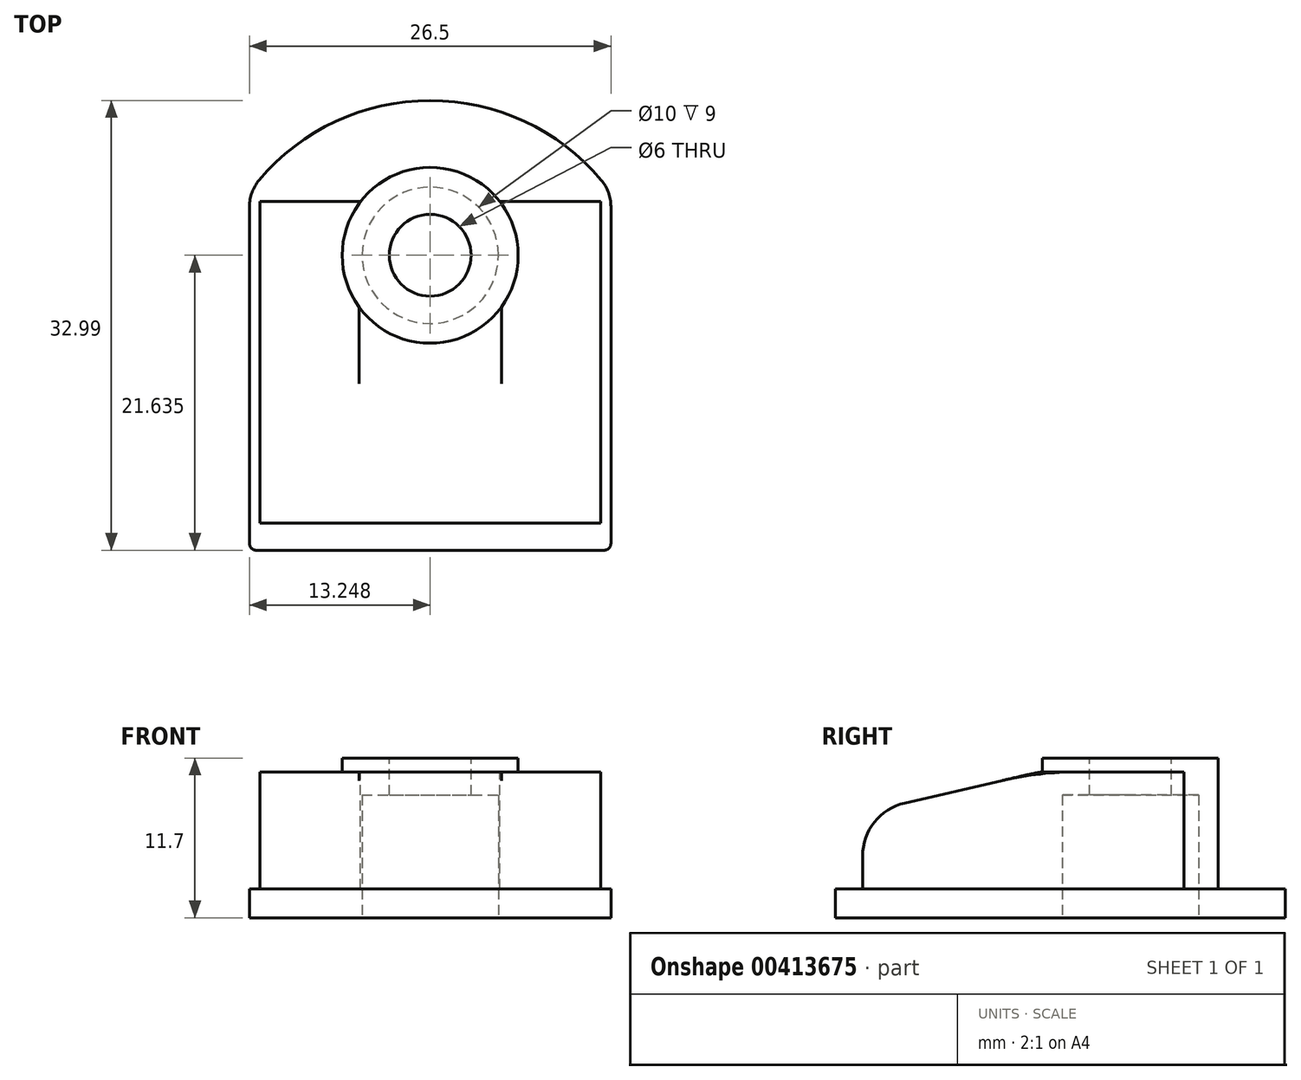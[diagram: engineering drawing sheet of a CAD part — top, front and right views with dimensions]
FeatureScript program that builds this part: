
annotation { "Feature Type Name" : "Feature", "Feature Type Description" : "" }
export const myFeature = defineFeature(function(context is Context, id is Id, definition is map)
    precondition{}
    {
        {
            var Q0;
            Q0=qCreatedBy(makeId("Top.planeOp"),FACE);
            var sketch = newSketch(context, id + "F0", { "sketchPlane" : qUnion([Q0])});
            skLineSegment(sketch, "E0", {"start": v(-15.11, -22.23) * mm, "end": v(11.39, -22.23) * mm});
            skLineSegment(sketch, "E1", {"start": v(11.39, -22.23) * mm, "end": v(11.39, 4.02) * mm});
            skLineSegment(sketch, "E2", {"start": v(-15.11, -22.23) * mm, "end": v(-15.11, 4.02) * mm});
            skArc(sketch, "E3", {"start": v(11.39, 4.02) * mm, "mid": v(-1.86, 10.76) * mm, "end": v(-15.11, 4.02) * mm});
            skSolve(sketch);
        }
        {
            var Q0;
            Q0 = qSketchRegion(id + "F0", true);
            extrude(context, id + "F1", {"entities" : qUnion([Q0]), "depth" : 2.1 * mm, "offsetDistance" : 25 * mm});
        }
        {
            var Q0;
            Q0=makeQuery(id+"F1.opExtrude","SWEPT_EDGE",EDGE,{"disambiguationData":[OSD([sQuery(id+"F0.wireOp",EDGE,"E0"),sQuery(id+"F0.wireOp",EDGE,"E2")])]});
            var Q1;
            Q1=makeQuery(id+"F1.opExtrude","SWEPT_EDGE",EDGE,{"disambiguationData":[OSD([sQuery(id+"F0.wireOp",EDGE,"E0"),sQuery(id+"F0.wireOp",EDGE,"E1")])]});
            fillet(context, id + "F2", {"entities" : qUnion([Q0, Q1]), "tangentPropagation" : true, "radius" : .5 * mm, "defaultsChanged" : true, "vertexSettings" : [], "allowEdgeOverflow" : false});
        }
        {
            var Q0;
            Q0=makeQuery(id+"F1.opExtrude","SWEPT_EDGE",EDGE,{"disambiguationData":[OSD([sQuery(id+"F0.wireOp",EDGE,"E1"),sQuery(id+"F0.wireOp",EDGE,"E3")])]});
            var Q1;
            Q1=makeQuery(id+"F1.opExtrude","SWEPT_EDGE",EDGE,{"disambiguationData":[OSD([sQuery(id+"F0.wireOp",EDGE,"E2"),sQuery(id+"F0.wireOp",EDGE,"E3")])]});
            fillet(context, id + "F3", {"entities" : qUnion([Q0, Q1]), "tangentPropagation" : true, "radius" : 3 * mm, "defaultsChanged" : true, "vertexSettings" : [], "allowEdgeOverflow" : false});
        }
        {
            var Q0;
            Q0=makeQuery(id+"F1.opExtrude","CAP_FACE",FACE,{"disambiguationData":[OSD([sQuery(id+"F0.wireOp",EDGE,"E0"),sQuery(id+"F0.wireOp",EDGE,"E1"),sQuery(id+"F0.wireOp",EDGE,"E2"),sQuery(id+"F0.wireOp",EDGE,"E3")])],"isStart":false});
            var sketch = newSketch(context, id + "F4", { "sketchPlane" : qUnion([Q0])});
            skLineSegment(sketch, "E4.0", {"start": v(10.64, -20.23) * mm, "end": v(10.64, 3.35) * mm});
            skLineSegment(sketch, "E4.2", {"start": v(-14.36, 3.35) * mm, "end": v(-14.36, -20.23) * mm});
            skLineSegment(sketch, "E5.0", {"start": v(-14.36, -20.23) * mm, "end": v(10.64, -20.23) * mm});
            skLineSegment(sketch, "E6", {"start": v(-14.36, 3.35) * mm, "end": v(10.64, 3.35) * mm});
            skSolve(sketch);
        }
        {
            var Q0;
            Q0 = qSketchRegion(id + "F4", true);
            extrude(context, id + "F5", {"entities" : qUnion([Q0]), "operationType" : NewBodyOperationType.ADD, "depth" : 8.6 * mm, "offsetDistance" : 25 * mm});
        }
        {
            var Q0;
            Q0=makeQuery(id+"F9.boolean.opBoolean","MERGE",FACE,{"derivedFrom":[makeQuery(id+"F5.opExtrude","CAP_FACE",FACE,{"disambiguationData":[OSD([sQuery(id+"F4.wireOp",EDGE,"E4.0"),sQuery(id+"F4.wireOp",EDGE,"E4.2"),sQuery(id+"F4.wireOp",EDGE,"E5.0"),sQuery(id+"F4.wireOp",EDGE,"E6")])],"isStart":false}),makeQuery(id+"F9.opExtrude","CAP_FACE",FACE,{"disambiguationData":[OSD([sQuery(id+"F8.wireOp",EDGE,"E8")])],"isStart":true})]});
            var sketch = newSketch(context, id + "F6", { "sketchPlane" : qUnion([Q0])});
            skCircle(sketch, "E7", {"center": v(-1.86, -0.6) * mm, "radius": 6.45 * mm});
            skSolve(sketch);
        }
        {
            var Q0;
            Q0 = qSketchRegion(id + "F6", true);
            extrude(context, id + "F7", {"entities" : qUnion([Q0]), "operationType" : NewBodyOperationType.ADD, "depth" : 1 * mm, "offsetDistance" : 25 * mm});
        }
        {
            var Q0;
            Q0=makeQuery(id+"F5.opExtrude","CAP_FACE",FACE,{"disambiguationData":[OSD([sQuery(id+"F4.wireOp",EDGE,"E4.0"),sQuery(id+"F4.wireOp",EDGE,"E4.2"),sQuery(id+"F4.wireOp",EDGE,"E5.0"),sQuery(id+"F4.wireOp",EDGE,"E6")])],"isStart":false});
            var sketch = newSketch(context, id + "F8", { "sketchPlane" : qUnion([Q0])});
            skCircle(sketch, "E8", {"center": v(-1.86, -0.6) * mm, "radius": 6.45 * mm});
            skLineSegment(sketch, "E9", {"start": v(-1.86, -20.23) * mm, "end": v(-1.86, 14.52) * mm, "construction": true});
            skSolve(sketch);
        }
        {
            var Q0;
            Q0 = qSketchRegion(id + "F8", true);
            extrude(context, id + "F9", {"entities" : qUnion([Q0]), "operationType" : NewBodyOperationType.ADD, "oppositeDirection" : true, "depth" : 10.7 * mm, "offsetDistance" : 25 * mm});
        }
        {
            var Q0;
            Q0=makeQuery(id+"F1.opExtrude","CAP_FACE",FACE,{"disambiguationData":[OSD([sQuery(id+"F0.wireOp",EDGE,"E0"),sQuery(id+"F0.wireOp",EDGE,"E1"),sQuery(id+"F0.wireOp",EDGE,"E2"),sQuery(id+"F0.wireOp",EDGE,"E3")])],"isStart":true});
            var sketch = newSketch(context, id + "F10", { "sketchPlane" : qUnion([Q0])});
            skCircle(sketch, "E10", {"center": v(-1.86, 0.6) * mm, "radius": 5 * mm});
            skSolve(sketch);
        }
        {
            var Q0;
            Q0 = qSketchRegion(id + "F10", true);
            extrude(context, id + "F11", {"entities" : qUnion([Q0]), "operationType" : NewBodyOperationType.REMOVE, "oppositeDirection" : true, "depth" : 9 * mm, "offsetDistance" : 25 * mm});
        }
        {
            var Q0;
            Q0=makeQuery(id+"F7.opExtrude","CAP_FACE",FACE,{"disambiguationData":[OSD([sQuery(id+"F6.wireOp",EDGE,"E7")])],"isStart":false});
            var sketch = newSketch(context, id + "F12", { "sketchPlane" : qUnion([Q0])});
            skCircle(sketch, "E11", {"center": v(-1.86, -0.6) * mm, "radius": 3 * mm});
            skSolve(sketch);
        }
        {
            var Q0;
            Q0 = qSketchRegion(id + "F12", true);
            extrude(context, id + "F13", {"entities" : qUnion([Q0]), "operationType" : NewBodyOperationType.REMOVE, "oppositeDirection" : true, "depth" : 25 * mm, "offsetDistance" : 25 * mm});
        }
        {
            var Q0;
            Q0=makeQuery(id+"F5.opExtrude","CAP_EDGE",EDGE,{"disambiguationData":[OSD([sQuery(id+"F4.wireOp",EDGE,"E5.0")])],"isStart":false});
            chamfer(context, id + "F14", {"entities" : qUnion([Q0]), "chamferType" : ChamferType.TWO_OFFSETS, "width1" : 13 * mm, "oppositeDirection" : false, "width2" : 3 * mm, "tangentPropagation" : true});
        }
        {
            var Q0;
            {var subQ0=sQuery(id+"F4.wireOp",EDGE,"E5.0");Q0=makeQuery(id+"F14.opChamfer","BLEND_EDGE",EDGE,{"blendedFrom":[makeQuery(id+"F5.opExtrude","CAP_EDGE",EDGE,{"disambiguationData":[OSD([subQ0])],"isStart":false}),makeQuery(id+"F5.opExtrude","SWEPT_FACE",FACE,{"disambiguationData":[OSD([subQ0])]})],"blendedInto":[makeQuery(id+"F5.opExtrude","SWEPT_FACE",FACE,{"disambiguationData":[OSD([subQ0])]})]});}
            fillet(context, id + "F15", {"entities" : qUnion([Q0]), "tangentPropagation" : true, "radius" : 4 * mm, "defaultsChanged" : true, "vertexSettings" : [], "allowEdgeOverflow" : false});
        }
        {
            var Q0;
            {var subQ0=sQuery(id+"F4.wireOp",EDGE,"E5.0");Q0=makeQuery(id+"F14.opChamfer","BLEND_EDGE",EDGE,{"blendedFrom":[makeQuery(id+"F5.opExtrude","CAP_EDGE",EDGE,{"disambiguationData":[OSD([subQ0])],"isStart":false}),makeQuery(id+"F5.opExtrude","CAP_FACE",FACE,{"disambiguationData":[OSD([sQuery(id+"F4.wireOp",EDGE,"E4.0"),sQuery(id+"F4.wireOp",EDGE,"E4.2"),subQ0,sQuery(id+"F4.wireOp",EDGE,"E6")])],"isStart":false})],"blendedInto":[makeQuery(id+"F5.opExtrude","CAP_FACE",FACE,{"disambiguationData":[OSD([sQuery(id+"F4.wireOp",EDGE,"E4.0"),sQuery(id+"F4.wireOp",EDGE,"E4.2"),subQ0,sQuery(id+"F4.wireOp",EDGE,"E6")])],"isStart":false})]});}
            fillet(context, id + "F16", {"entities" : qUnion([Q0]), "tangentPropagation" : true, "radius" : 25 * mm, "defaultsChanged" : true, "vertexSettings" : [], "allowEdgeOverflow" : false});
        }
    });
